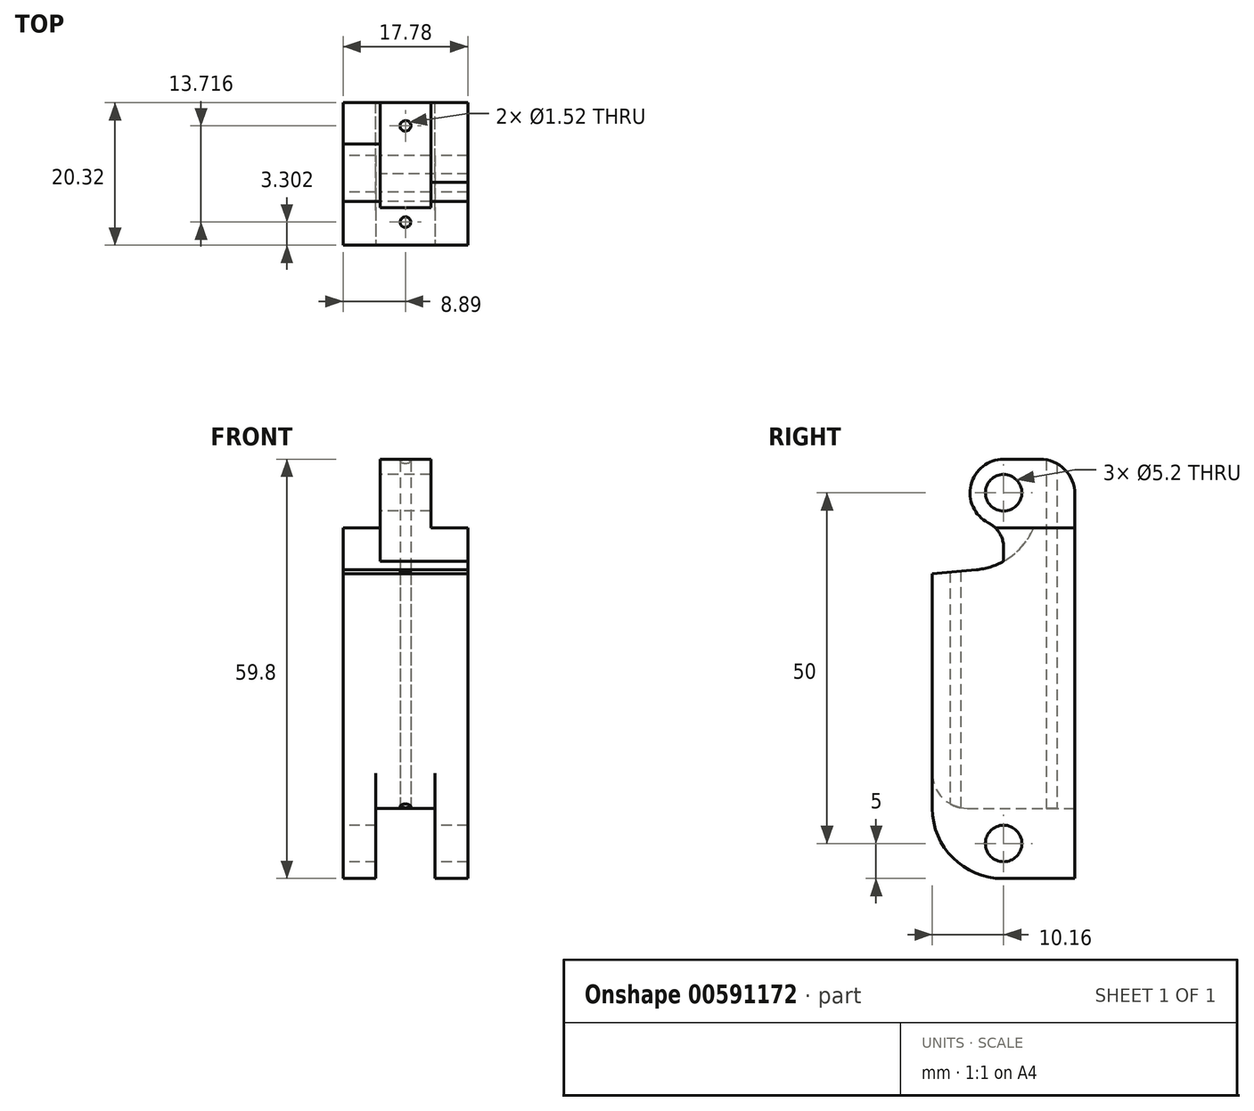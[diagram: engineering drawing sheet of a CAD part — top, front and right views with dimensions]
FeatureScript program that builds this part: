
annotation { "Feature Type Name" : "Feature", "Feature Type Description" : "" }
export const myFeature = defineFeature(function(context is Context, id is Id, definition is map)
    precondition{}
    {
        {
            var Q0;
            Q0=qCreatedBy(makeId("Front.planeOp"),FACE);
            var sketch = newSketch(context, id + "F0", { "sketchPlane" : qUnion([Q0])});
            skLineSegment(sketch, "E0.bottom", {"start": v(8.9, 25) * mm, "end": v(3.61, 25) * mm});
            skLineSegment(sketch, "E0.top", {"start": v(8.9, -25) * mm, "end": v(4.21, -25) * mm});
            skLineSegment(sketch, "E0.left", {"start": v(8.89, 25) * mm, "end": v(8.89, -25) * mm});
            skLineSegment(sketch, "E0.right", {"start": v(-8.9, 25) * mm, "end": v(-8.9, -25) * mm});
            skPoint(sketch, "E0.middle", {"position": v(0, 0) * mm});
            skLineSegment(sketch, "E1.left", {"start": v(4.21, -25) * mm, "end": v(4.21, -15) * mm});
            skLineSegment(sketch, "E1.right", {"start": v(-4.21, -25) * mm, "end": v(-4.21, -15) * mm});
            skLineSegment(sketch, "E2", {"start": v(0, -15) * mm, "end": v(4.21, -15) * mm});
            skLineSegment(sketch, "E3", {"start": v(0, -15) * mm, "end": v(-4.21, -15) * mm});
            skLineSegment(sketch, "E4.trimOffspring", {"start": v(-4.21, -25) * mm, "end": v(-8.9, -25) * mm});
            skLineSegment(sketch, "E5.bottom", {"start": v(3.6, 34.8) * mm, "end": v(-3.61, 34.8) * mm});
            skLineSegment(sketch, "E5.left", {"start": v(3.6, 34.8) * mm, "end": v(3.6, 25) * mm});
            skLineSegment(sketch, "E5.right", {"start": v(-3.61, 34.8) * mm, "end": v(-3.61, 25) * mm});
            skPoint(sketch, "E5.middle", {"position": v(0, 25) * mm});
            skLineSegment(sketch, "E6.trimOffspring", {"start": v(-3.61, 25) * mm, "end": v(-8.9, 25) * mm});
            skPoint(sketch, "E7.orphan", {"position": v(-3.6, 15.2) * mm});
            skPoint(sketch, "E8.orphan", {"position": v(3.6, 15.2) * mm});
            skSolve(sketch);
        }
        {
            var Q0;
            Q0=makeQuery(id+"F0.imprint","IMPRINT",FACE,{"disambiguationData":[TD([[makeQuery(id+"F0.imprint","IMPRINT",EDGE,{"derivedFrom":sQuery(id+"F0.wireOp",EDGE,"E0.bottom")}),1.0]])]});
            extrude(context, id + "F1", {"entities" : qUnion([Q0]), "depth" : 20.32 * mm, "offsetDistance" : 25.4 * mm, "symmetric" : true});
        }
        {
            var Q0;
            Q0=makeQuery(id+"F1.opExtrude","SWEPT_FACE",FACE,{"disambiguationData":[OSD([sQuery(id+"F0.wireOp",EDGE,"E0.right")])]});
            var sketch = newSketch(context, id + "F2", { "sketchPlane" : qUnion([Q0])});
            skPoint(sketch, "E9.endSnap0", {"position": v(0, -25) * mm});
            skCircle(sketch, "E10", {"center": v(0, -20) * mm, "radius": 2.6 * mm});
            skSolve(sketch);
        }
        {
            var Q0;
            Q0=makeQuery(id+"F2.imprint","IMPRINT",FACE,{"disambiguationData":[TD([[makeQuery(id+"F2.imprint","IMPRINT",EDGE,{"derivedFrom":sQuery(id+"F2.wireOp",EDGE,"E10")}),1.0]])]});
            extrude(context, id + "F3", {"entities" : qUnion([Q0]), "operationType" : NewBodyOperationType.REMOVE, "endBound" : BoundingType.THROUGH_ALL, "oppositeDirection" : true, "depth" : 25.4 * mm, "offsetDistance" : 25.4 * mm});
        }
        {
            var Q0;
            Q0=makeQuery(id+"F1.opExtrude","SWEPT_FACE",FACE,{"disambiguationData":[OSD([sQuery(id+"F0.wireOp",EDGE,"E0.right")])]});
            var sketch = newSketch(context, id + "F4", { "sketchPlane" : qUnion([Q0])});
            skLineSegment(sketch, "E11", {"start": v(10.16, 25) * mm, "end": v(-4.3, 25) * mm});
            skLineSegment(sketch, "E12", {"start": v(10.16, 25) * mm, "end": v(10.16, 18.47) * mm});
            skLineSegment(sketch, "E13", {"start": v(10.16, 18.47) * mm, "end": v(3.89, 19.02) * mm});
            skPoint(sketch, "E14.visualSharp", {"position": v(-2.14, 14.35) * mm});
            skArc(sketch, "E14.filletArc", {"start": v(-4.3, 25) * mm, "mid": v(-1.02, 20.9) * mm, "end": v(3.89, 19.02) * mm});
            skSolve(sketch);
        }
        {
            var Q0;
            Q0=makeQuery(id+"F4.imprint","IMPRINT",FACE,{"disambiguationData":[TD([[makeQuery(id+"F4.imprint","IMPRINT",EDGE,{"derivedFrom":sQuery(id+"F4.wireOp",EDGE,"E11")}),1.0]])]});
            extrude(context, id + "F5", {"entities" : qUnion([Q0]), "operationType" : NewBodyOperationType.REMOVE, "oppositeDirection" : true, "depth" : 5.08 * mm + .2 * mm, "offsetDistance" : 25.4 * mm});
        }
        {
            var Q0;
            Q0=makeQuery(id+"F1.opExtrude","CAP_EDGE",EDGE,{"disambiguationData":[OSD([sQuery(id+"F0.wireOp",EDGE,"E0.top")])],"isStart":false});
            var Q1;
            Q1=makeQuery(id+"F1.opExtrude","CAP_EDGE",EDGE,{"disambiguationData":[OSD([sQuery(id+"F0.wireOp",EDGE,"E4.trimOffspring")])],"isStart":false});
            fillet(context, id + "F6", {"entities" : qUnion([Q0, Q1]), "radius" : 10 * mm, "tangentPropagation" : true, "allowEdgeOverflow" : false});
        }
        {
            var Q0;
            Q0=makeQuery(id+"F5.boolean.opBoolean","MERGE",FACE,{"derivedFrom":[makeQuery(id+"F1.opExtrude","SWEPT_FACE",FACE,{"disambiguationData":[OSD([sQuery(id+"F0.wireOp",EDGE,"E5.right")])]}),makeQuery(id+"F5.opExtrude","CAP_FACE",FACE,{"disambiguationData":[OSD([sQuery(id+"F4.wireOp",EDGE,"E11"),sQuery(id+"F4.wireOp",EDGE,"E12"),sQuery(id+"F4.wireOp",EDGE,"E13"),sQuery(id+"F4.wireOp",EDGE,"E14.filletArc")])],"isStart":false})]});
            var sketch = newSketch(context, id + "F7", { "sketchPlane" : qUnion([Q0])});
            skLineSegment(sketch, "E15", {"start": v(0, 25) * mm, "end": v(0, 25.2) * mm});
            skCircle(sketch, "E16", {"center": v(0, 30) * mm, "radius": 2.6 * mm});
            skArc(sketch, "E17", {"start": v(0, 25.2) * mm, "mid": v(4.8, 30) * mm, "end": v(0, 34.8) * mm});
            skLineSegment(sketch, "E18", {"start": v(0, 34.8) * mm, "end": v(10.16, 34.8) * mm});
            skLineSegment(sketch, "E19", {"start": v(10.16, 34.8) * mm, "end": v(10.16, 18.47) * mm});
            skLineSegment(sketch, "E20", {"start": v(0, 25) * mm, "end": v(0, 20.25) * mm});
            skArc(sketch, "E21", {"start": v(0, 20.25) * mm, "mid": v(2, 19.4) * mm, "end": v(4.14, 19) * mm});
            skPoint(sketch, "E21.first.point", {"position": v(-4.3, 25) * mm});
            skPoint(sketch, "E21.third.point", {"position": v(13.07, 34.71) * mm});
            skLineSegment(sketch, "E22", {"start": v(10.16, 18.47) * mm, "end": v(3.89, 19.02) * mm});
            skArc(sketch, "E23.trimOffspring", {"start": v(-4.3, 25) * mm, "mid": v(-1.02, 20.9) * mm, "end": v(3.89, 19.02) * mm});
            skSolve(sketch);
        }
        {
            var Q0;
            Q0=makeQuery(id+"F7.imprint","IMPRINT",FACE,{"disambiguationData":[TD([[makeQuery(id+"F7.imprint","IMPRINT",EDGE,{"derivedFrom":sQuery(id+"F7.wireOp",EDGE,"E16")}),1.0]])]});
            var Q1;
            Q1=makeQuery(id+"F7.imprint","IMPRINT",FACE,{"disambiguationData":[TD([[makeQuery(id+"F7.imprint","IMPRINT",EDGE,{"derivedFrom":sQuery(id+"F7.wireOp",EDGE,"E15")}),-1.0]])]});
            extrude(context, id + "F8", {"entities" : qUnion([Q0, Q1]), "operationType" : NewBodyOperationType.REMOVE, "endBound" : BoundingType.THROUGH_ALL, "oppositeDirection" : true, "depth" : 25.4 * mm, "offsetDistance" : 25.4 * mm});
        }
        {
            var Q0;
            Q0=makeQuery(id+"F8.boolean.opBoolean","COPY",EDGE,{"derivedFrom":makeQuery(id+"F8.opExtrude","SWEPT_EDGE",EDGE,{"disambiguationData":[OSD([sQuery(id+"F7.wireOp",EDGE,"E15"),sQuery(id+"F7.wireOp",EDGE,"E17")])]})});
            var Q1;
            Q1=makeQuery(id+"F8.boolean.opBoolean","COPY",EDGE,{"derivedFrom":makeQuery(id+"F8.opExtrude","SWEPT_EDGE",EDGE,{"disambiguationData":[OSD([sQuery(id+"F7.wireOp",EDGE,"E20"),sQuery(id+"F7.wireOp",EDGE,"E22")])]})});
            fillet(context, id + "F9", {"entities" : qUnion([Q0, Q1]), "radius" : 4 * mm, "tangentPropagation" : true, "allowEdgeOverflow" : false});
        }
        {
            var Q0;
            Q0=makeQuery(id+"F1.opExtrude","CAP_EDGE",EDGE,{"disambiguationData":[OSD([sQuery(id+"F0.wireOp",EDGE,"E5.bottom")])],"isStart":true});
            fillet(context, id + "F10", {"entities" : qUnion([Q0]), "radius" : 5 * mm, "tangentPropagation" : true, "allowEdgeOverflow" : false});
        }
        {
            var Q0;
            Q0=makeQuery(id+"F1.opExtrude","CAP_EDGE",EDGE,{"disambiguationData":[OSD([sQuery(id+"F0.wireOp",EDGE,"E2"),sQuery(id+"F0.wireOp",EDGE,"E3")])],"isStart":false});
            fillet(context, id + "F11", {"entities" : qUnion([Q0]), "radius" : 5 * mm, "tangentPropagation" : true, "allowEdgeOverflow" : false});
        }
        {
            var Q0;
            Q0=makeQuery(id+"F1.opExtrude","SWEPT_FACE",FACE,{"disambiguationData":[OSD([sQuery(id+"F0.wireOp",EDGE,"E2"),sQuery(id+"F0.wireOp",EDGE,"E3")])]});
            var sketch = newSketch(context, id + "F12", { "sketchPlane" : qUnion([Q0])});
            skLineSegment(sketch, "E24", {"start": v(0, -10.16) * mm, "end": v(0, -7.62) * mm});
            skPoint(sketch, "E24.endSnap0", {"position": v(0, -10.16) * mm});
            skCircle(sketch, "E25", {"center": v(0, -6.86) * mm, "radius": 0.76 * mm});
            skLineSegment(sketch, "E26", {"start": v(0, 10.16) * mm, "end": v(0, 7.62) * mm});
            skCircle(sketch, "E27", {"center": v(0, 6.86) * mm, "radius": 0.76 * mm});
            skLineSegment(sketch, "E28", {"start": v(-8.9, 10.16) * mm, "end": v(8.89, 10.16) * mm});
            skSolve(sketch);
        }
        {
            var Q0;
            Q0=makeQuery(id+"F12.imprint","IMPRINT",FACE,{"disambiguationData":[TD([[makeQuery(id+"F12.imprint","IMPRINT",EDGE,{"derivedFrom":sQuery(id+"F12.wireOp",EDGE,"E27")}),1.0]])]});
            var Q1;
            Q1=makeQuery(id+"F12.imprint","IMPRINT",FACE,{"disambiguationData":[TD([[makeQuery(id+"F12.imprint","IMPRINT",EDGE,{"derivedFrom":sQuery(id+"F12.wireOp",EDGE,"E25")}),1.0]])]});
            var Q2;
            {var subQ0=sQuery(id+"F12.wireOp",EDGE,"E27");var subQ1=sQuery(id+"F0.wireOp",EDGE,"E3");var subQ2=sQuery(id+"F0.wireOp",EDGE,"E2");var subQ3=makeQuery(id+"F11.opFillet","BLEND_EDGE",EDGE,{"blendedFrom":[makeQuery(id+"F1.opExtrude","CAP_EDGE",EDGE,{"disambiguationData":[OSD([subQ2,subQ1])],"isStart":false}),makeQuery(id+"F1.opExtrude","SWEPT_FACE",FACE,{"disambiguationData":[OSD([subQ2,subQ1])]})],"blendedInto":[makeQuery(id+"F1.opExtrude","SWEPT_FACE",FACE,{"disambiguationData":[OSD([subQ2,subQ1])]})]});var subQ4=makeQuery(id+"F12.imprint","INTERSECT",VERTEX,{"disambiguationData":[OD(0.0)],"derivedFrom":[subQ3,subQ0]});Q2=makeQuery(id+"F12.imprint","IMPRINT",FACE,{"disambiguationData":[TD([[makeQuery(id+"F12.imprint","IMPRINT",EDGE,{"disambiguationData":[TD([[subQ4,-1.0]])],"derivedFrom":subQ0}),1.0]])]});}
            extrude(context, id + "F13", {"entities" : qUnion([Q0, Q1, Q2]), "operationType" : NewBodyOperationType.REMOVE, "endBound" : BoundingType.THROUGH_ALL, "oppositeDirection" : true, "depth" : 25.4 * mm, "offsetDistance" : 25.4 * mm});
        }
    });
